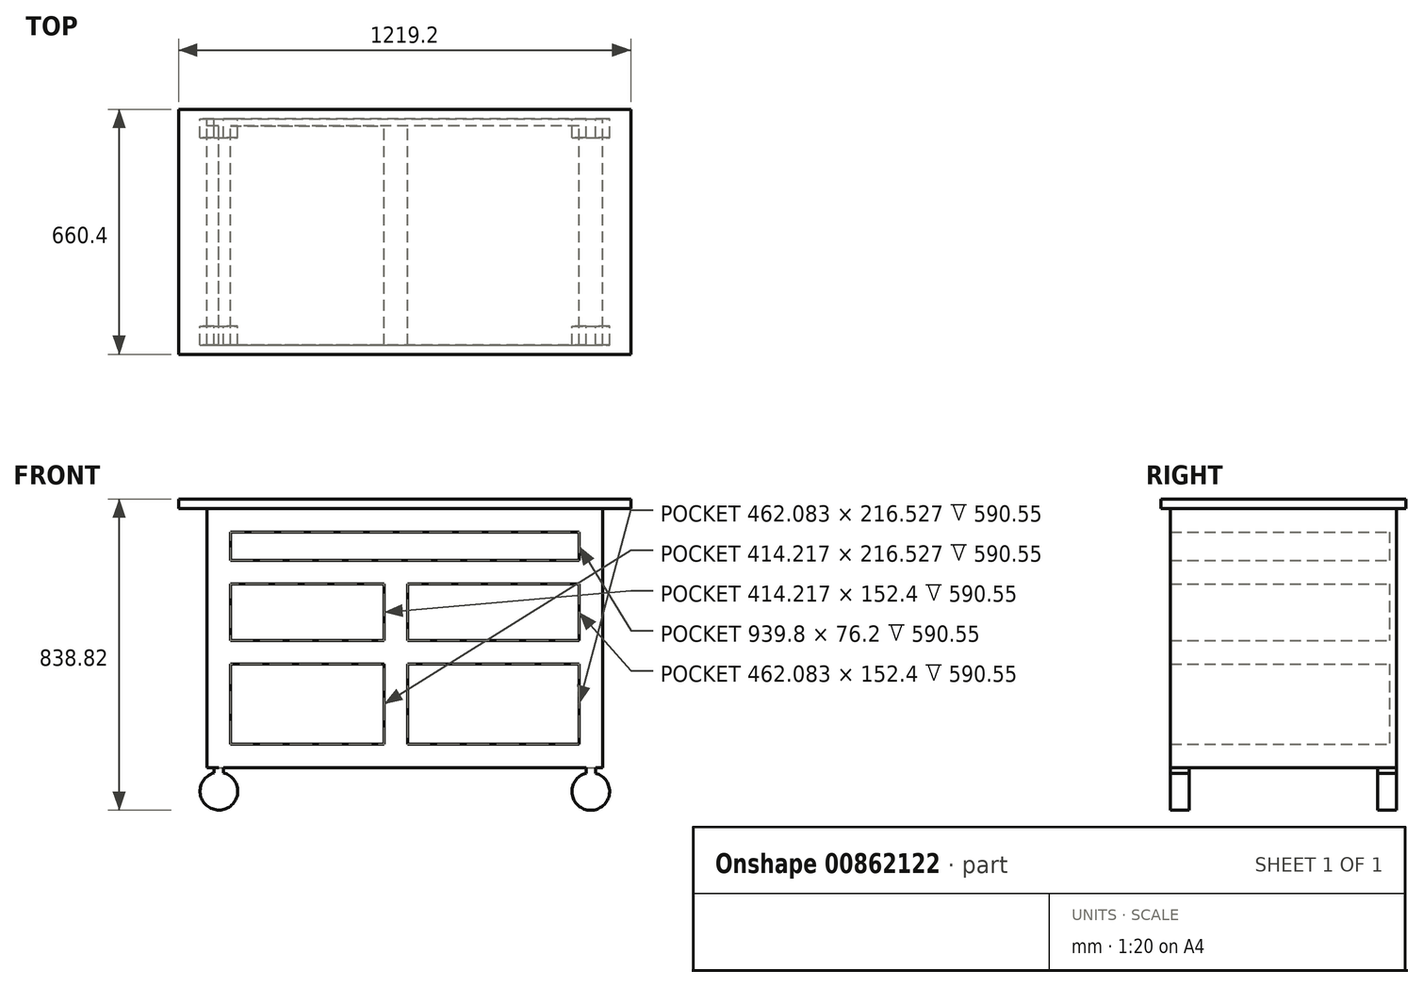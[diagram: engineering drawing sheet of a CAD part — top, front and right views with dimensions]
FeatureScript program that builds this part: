
annotation { "Feature Type Name" : "Feature", "Feature Type Description" : "" }
export const myFeature = defineFeature(function(context is Context, id is Id, definition is map)
    precondition{}
    {
        {
            var Q0;
            Q0=qCreatedBy(makeId("Front.planeOp"),FACE);
            var sketch = newSketch(context, id + "F0", { "sketchPlane" : qUnion([Q0])});
            skLineSegment(sketch, "E0.bottom", {"start": v(533.4, -317.81) * mm, "end": v(-533.4, -317.81) * mm});
            skLineSegment(sketch, "E0.top", {"start": v(533.4, 317.81) * mm, "end": v(-533.4, 317.81) * mm});
            skLineSegment(sketch, "E0.left", {"start": v(533.4, -317.81) * mm, "end": v(533.4, 317.81) * mm});
            skLineSegment(sketch, "E0.right", {"start": v(-533.4, -317.81) * mm, "end": v(-533.4, 317.81) * mm});
            skPoint(sketch, "E0.middle", {"position": v(0, 0) * mm});
            skLineSegment(sketch, "E1.top", {"start": v(469.9, 317.81) * mm, "end": v(-469.9, 317.81) * mm});
            skLineSegment(sketch, "E1.left", {"start": v(469.9, -317.81) * mm, "end": v(469.9, 317.81) * mm});
            skLineSegment(sketch, "E1.right", {"start": v(-469.9, -317.81) * mm, "end": v(-469.9, 317.81) * mm});
            skLineSegment(sketch, "E2.bottom", {"start": v(-533.4, 317.81) * mm, "end": v(533.4, 317.81) * mm});
            skLineSegment(sketch, "E2.top", {"start": v(-533.4, 381.31) * mm, "end": v(533.4, 381.31) * mm});
            skLineSegment(sketch, "E2.left", {"start": v(-533.4, 317.81) * mm, "end": v(-533.4, 381.31) * mm});
            skLineSegment(sketch, "E2.right", {"start": v(533.4, 317.81) * mm, "end": v(533.4, 381.31) * mm});
            skCircle(sketch, "E3", {"center": v(-500.76, -380.69) * mm, "radius": 50.8 * mm});
            skCircle(sketch, "E4", {"center": v(501.65, -381.31) * mm, "radius": 50.8 * mm});
            skLineSegment(sketch, "E5.top", {"start": v(-469.9, -254.31) * mm, "end": v(469.9, -254.31) * mm});
            skLineSegment(sketch, "E5.left", {"start": v(-469.9, -317.81) * mm, "end": v(-469.9, -254.31) * mm});
            skLineSegment(sketch, "E5.right", {"start": v(469.9, -273.37) * mm, "end": v(469.9, -254.31) * mm});
            skLineSegment(sketch, "E6.bottom", {"start": v(-469.9, 241.61) * mm, "end": v(469.9, 241.61) * mm});
            skLineSegment(sketch, "E6.top", {"start": v(-469.9, 178.11) * mm, "end": v(469.9, 178.11) * mm});
            skLineSegment(sketch, "E6.left", {"start": v(-469.9, 241.61) * mm, "end": v(-469.9, 178.11) * mm});
            skLineSegment(sketch, "E6.right", {"start": v(469.9, 241.61) * mm, "end": v(469.9, 178.11) * mm});
            skLineSegment(sketch, "E7.bottom", {"start": v(469.9, 25.71) * mm, "end": v(-469.9, 25.71) * mm});
            skLineSegment(sketch, "E7.top", {"start": v(469.9, -37.79) * mm, "end": v(-469.9, -37.79) * mm});
            skLineSegment(sketch, "E7.left", {"start": v(469.9, 25.71) * mm, "end": v(469.9, -37.79) * mm});
            skLineSegment(sketch, "E7.right", {"start": v(-469.9, 25.71) * mm, "end": v(-469.9, -37.79) * mm});
            skLineSegment(sketch, "E8.bottom", {"start": v(-55.68, 178.11) * mm, "end": v(7.82, 178.11) * mm});
            skLineSegment(sketch, "E8.top", {"start": v(-55.68, -254.31) * mm, "end": v(7.82, -254.31) * mm});
            skLineSegment(sketch, "E8.left", {"start": v(-55.68, 178.11) * mm, "end": v(-55.68, -254.31) * mm});
            skLineSegment(sketch, "E8.right", {"start": v(7.82, 178.11) * mm, "end": v(7.82, -254.31) * mm});
            skLineSegment(sketch, "E9", {"start": v(-501.66, -317.2) * mm, "end": v(-500.76, -380.69) * mm});
            skLineSegment(sketch, "E10", {"start": v(501.65, -317.81) * mm, "end": v(501.65, -381.31) * mm});
            skLineSegment(sketch, "E11", {"start": v(-533.4, -317.81) * mm, "end": v(-501.66, -317.2) * mm});
            skLineSegment(sketch, "E12", {"start": v(533.4, -317.81) * mm, "end": v(501.65, -317.81) * mm});
            skLineSegment(sketch, "E13.bottom", {"start": v(-488.96, -342.6) * mm, "end": v(-514.36, -342.6) * mm});
            skLineSegment(sketch, "E13.top", {"start": v(-488.96, -291.8) * mm, "end": v(-514.36, -291.8) * mm});
            skLineSegment(sketch, "E13.left", {"start": v(-488.96, -342.6) * mm, "end": v(-488.96, -291.8) * mm});
            skLineSegment(sketch, "E13.right", {"start": v(-514.36, -342.6) * mm, "end": v(-514.36, -291.8) * mm});
            skPoint(sketch, "E13.middle", {"position": v(-501.66, -317.2) * mm});
            skLineSegment(sketch, "E14.bottom", {"start": v(514.35, -343.21) * mm, "end": v(488.95, -343.21) * mm});
            skLineSegment(sketch, "E14.top", {"start": v(514.35, -292.41) * mm, "end": v(488.95, -292.41) * mm});
            skLineSegment(sketch, "E14.left", {"start": v(514.35, -343.21) * mm, "end": v(514.35, -292.41) * mm});
            skLineSegment(sketch, "E14.right", {"start": v(488.95, -343.21) * mm, "end": v(488.95, -292.41) * mm});
            skPoint(sketch, "E14.middle", {"position": v(501.65, -317.81) * mm});
            skSolve(sketch);
        }
        {
            var Q0;
            {var subQ1=sQuery(id+"F0.wireOp",EDGE,"E0.right");Q0=makeQuery(id+"F0.imprint","IMPRINT",FACE,{"disambiguationData":[TD([[makeQuery(id+"F0.imprint","IMPRINT",EDGE,{"derivedFrom":subQ1}),-1.0]])]});}
            var Q1;
            Q1=makeQuery(id+"F0.imprint","IMPRINT",FACE,{"disambiguationData":[TD([[makeQuery(id+"F0.imprint","IMPRINT",EDGE,{"derivedFrom":sQuery(id+"F0.wireOp",EDGE,"E2.top")}),-1.0]])]});
            var Q2;
            {var subQ4=sQuery(id+"F0.wireOp",EDGE,"E6.bottom");Q2=makeQuery(id+"F0.imprint","IMPRINT",FACE,{"disambiguationData":[TD([[makeQuery(id+"F0.imprint","IMPRINT",EDGE,{"derivedFrom":subQ4}),-1.0]])]});}
            var Q3;
            {var subQ0=sQuery(id+"F0.wireOp",EDGE,"E7.top");var subQ1=sQuery(id+"F0.wireOp",EDGE,"E1.right");var subQ2=makeQuery(id+"F0.imprint","INTERSECT",VERTEX,{"derivedFrom":[subQ1,subQ0]});Q3=makeQuery(id+"F0.imprint","IMPRINT",FACE,{"disambiguationData":[TD([[makeQuery(id+"F0.imprint","IMPRINT",EDGE,{"disambiguationData":[TD([[subQ2,-1.0]])],"derivedFrom":subQ1}),-1.0]])]});}
            var Q4;
            {var subQ5=sQuery(id+"F0.wireOp",EDGE,"E1.left");var subQ7=makeQuery(id+"F0.imprint","IMPRINT",VERTEX,{"derivedFrom":subQ5});Q4=makeQuery(id+"F0.imprint","IMPRINT",FACE,{"disambiguationData":[TD([[makeQuery(id+"F0.imprint","IMPRINT",EDGE,{"disambiguationData":[TD([[subQ7,1.0]])],"derivedFrom":subQ5}),1.0]])]});}
            var Q5;
            {var subQ0=sQuery(id+"F0.wireOp",EDGE,"E8.right");var subQ1=sQuery(id+"F0.wireOp",EDGE,"E5.top");var subQ2=makeQuery(id+"F0.imprint","INTERSECT",VERTEX,{"derivedFrom":[subQ1,subQ0]});Q5=makeQuery(id+"F0.imprint","IMPRINT",FACE,{"disambiguationData":[TD([[makeQuery(id+"F0.imprint","IMPRINT",EDGE,{"disambiguationData":[TD([[subQ2,1.0]])],"derivedFrom":subQ1}),1.0]])]});}
            var Q6;
            {var subQ0=sQuery(id+"F0.wireOp",EDGE,"E8.left");var subQ1=sQuery(id+"F0.wireOp",EDGE,"E7.bottom");var subQ2=makeQuery(id+"F0.imprint","INTERSECT",VERTEX,{"derivedFrom":[subQ1,subQ0]});Q6=makeQuery(id+"F0.imprint","IMPRINT",FACE,{"disambiguationData":[TD([[makeQuery(id+"F0.imprint","IMPRINT",EDGE,{"disambiguationData":[TD([[subQ2,1.0]])],"derivedFrom":subQ1}),1.0]])]});}
            var Q7;
            {var subQ0=sQuery(id+"F0.wireOp",EDGE,"E8.right");var subQ1=sQuery(id+"F0.wireOp",EDGE,"E6.top");var subQ2=makeQuery(id+"F0.imprint","INTERSECT",VERTEX,{"derivedFrom":[subQ1,subQ0]});Q7=makeQuery(id+"F0.imprint","IMPRINT",FACE,{"disambiguationData":[TD([[makeQuery(id+"F0.imprint","IMPRINT",EDGE,{"disambiguationData":[TD([[subQ2,1.0]])],"derivedFrom":subQ1}),-1.0]])]});}
            var Q8;
            {var subQ0=sQuery(id+"F0.wireOp",EDGE,"E7.bottom");var subQ1=sQuery(id+"F0.wireOp",EDGE,"E1.left");var subQ2=makeQuery(id+"F0.imprint","INTERSECT",VERTEX,{"derivedFrom":[subQ1,subQ0]});Q8=makeQuery(id+"F0.imprint","IMPRINT",FACE,{"disambiguationData":[TD([[makeQuery(id+"F0.imprint","IMPRINT",EDGE,{"disambiguationData":[TD([[subQ2,1.0]])],"derivedFrom":subQ1}),1.0]])]});}
            var Q9;
            {var subQ12=sQuery(id+"F0.wireOp",EDGE,"E0.left");Q9=makeQuery(id+"F0.imprint","IMPRINT",FACE,{"disambiguationData":[TD([[makeQuery(id+"F0.imprint","IMPRINT",EDGE,{"derivedFrom":subQ12}),1.0]])]});}
            var Q10;
            {var subQ1=sQuery(id+"F0.wireOp",EDGE,"E14.top");Q10=makeQuery(id+"F0.imprint","IMPRINT",FACE,{"disambiguationData":[TD([[makeQuery(id+"F0.imprint","IMPRINT",EDGE,{"derivedFrom":subQ1}),1.0]])]});}
            var Q11;
            {var subQ0=sQuery(id+"F0.wireOp",EDGE,"E13.top");Q11=makeQuery(id+"F0.imprint","IMPRINT",FACE,{"disambiguationData":[TD([[makeQuery(id+"F0.imprint","IMPRINT",EDGE,{"derivedFrom":subQ0}),1.0]])]});}
            extrude(context, id + "F1", {"entities" : qUnion([Q0, Q1, Q2, Q3, Q4, Q5, Q6, Q7, Q8, Q9, Q10, Q11]), "depth" : 609.6 * mm, "offsetDistance" : 25.4 * mm});
        }
        {
            var Q0;
            {var subQ2=sQuery(id+"F0.wireOp",EDGE,"E13.left");var subQ4=sQuery(id+"F0.wireOp",EDGE,"E3");var subQ5=makeQuery(id+"F0.imprint","INTERSECT",VERTEX,{"derivedFrom":[subQ4,subQ2]});Q0=makeQuery(id+"F0.imprint","IMPRINT",FACE,{"disambiguationData":[TD([[makeQuery(id+"F0.imprint","IMPRINT",EDGE,{"disambiguationData":[TD([[subQ5,1.0]])],"derivedFrom":subQ4}),1.0]])]});}
            var Q1;
            {var subQ0=sQuery(id+"F0.wireOp",EDGE,"E13.right");var subQ1=sQuery(id+"F0.wireOp",EDGE,"E3");var subQ2=makeQuery(id+"F0.imprint","INTERSECT",VERTEX,{"derivedFrom":[subQ1,subQ0]});Q1=makeQuery(id+"F0.imprint","IMPRINT",FACE,{"disambiguationData":[TD([[makeQuery(id+"F0.imprint","IMPRINT",EDGE,{"disambiguationData":[TD([[subQ2,1.0]])],"derivedFrom":subQ1}),1.0]])]});}
            var Q2;
            {var subQ0=sQuery(id+"F0.wireOp",EDGE,"E9");var subQ1=sQuery(id+"F0.wireOp",EDGE,"E0.bottom");var subQ2=makeQuery(id+"F0.imprint","INTERSECT",VERTEX,{"derivedFrom":[subQ1,subQ0]});Q2=makeQuery(id+"F0.imprint","IMPRINT",FACE,{"disambiguationData":[TD([[makeQuery(id+"F0.imprint","IMPRINT",EDGE,{"disambiguationData":[TD([[subQ2,-1.0]])],"derivedFrom":subQ1}),1.0]])]});}
            var Q3;
            {var subQ0=sQuery(id+"F0.wireOp",EDGE,"E9");var subQ1=sQuery(id+"F0.wireOp",EDGE,"E0.bottom");var subQ2=makeQuery(id+"F0.imprint","INTERSECT",VERTEX,{"derivedFrom":[subQ1,subQ0]});Q3=makeQuery(id+"F0.imprint","IMPRINT",FACE,{"disambiguationData":[TD([[makeQuery(id+"F0.imprint","IMPRINT",EDGE,{"disambiguationData":[TD([[subQ2,1.0]])],"derivedFrom":subQ1}),1.0]])]});}
            var Q4;
            {var subQ0=sQuery(id+"F0.wireOp",EDGE,"E13.left");var subQ1=sQuery(id+"F0.wireOp",EDGE,"E3");var subQ2=makeQuery(id+"F0.imprint","INTERSECT",VERTEX,{"derivedFrom":[subQ1,subQ0]});Q4=makeQuery(id+"F0.imprint","IMPRINT",FACE,{"disambiguationData":[TD([[makeQuery(id+"F0.imprint","IMPRINT",EDGE,{"disambiguationData":[TD([[subQ2,-1.0]])],"derivedFrom":subQ1}),1.0]])]});}
            var Q5;
            {var subQ2=sQuery(id+"F0.wireOp",EDGE,"E14.left");var subQ4=sQuery(id+"F0.wireOp",EDGE,"E4");var subQ5=makeQuery(id+"F0.imprint","INTERSECT",VERTEX,{"derivedFrom":[subQ4,subQ2]});Q5=makeQuery(id+"F0.imprint","IMPRINT",FACE,{"disambiguationData":[TD([[makeQuery(id+"F0.imprint","IMPRINT",EDGE,{"disambiguationData":[TD([[subQ5,1.0]])],"derivedFrom":subQ4}),1.0]])]});}
            var Q6;
            {var subQ0=sQuery(id+"F0.wireOp",EDGE,"E14.left");var subQ1=sQuery(id+"F0.wireOp",EDGE,"E4");var subQ2=makeQuery(id+"F0.imprint","INTERSECT",VERTEX,{"derivedFrom":[subQ1,subQ0]});Q6=makeQuery(id+"F0.imprint","IMPRINT",FACE,{"disambiguationData":[TD([[makeQuery(id+"F0.imprint","IMPRINT",EDGE,{"disambiguationData":[TD([[subQ2,-1.0]])],"derivedFrom":subQ1}),1.0]])]});}
            var Q7;
            {var subQ0=sQuery(id+"F0.wireOp",EDGE,"E14.right");var subQ1=sQuery(id+"F0.wireOp",EDGE,"E0.bottom");var subQ2=makeQuery(id+"F0.imprint","INTERSECT",VERTEX,{"derivedFrom":[subQ1,subQ0]});Q7=makeQuery(id+"F0.imprint","IMPRINT",FACE,{"disambiguationData":[TD([[makeQuery(id+"F0.imprint","IMPRINT",EDGE,{"disambiguationData":[TD([[subQ2,1.0]])],"derivedFrom":subQ1}),1.0]])]});}
            var Q8;
            {var subQ0=sQuery(id+"F0.wireOp",EDGE,"E14.left");var subQ1=sQuery(id+"F0.wireOp",EDGE,"E0.bottom");var subQ2=makeQuery(id+"F0.imprint","INTERSECT",VERTEX,{"derivedFrom":[subQ1,subQ0]});Q8=makeQuery(id+"F0.imprint","IMPRINT",FACE,{"disambiguationData":[TD([[makeQuery(id+"F0.imprint","IMPRINT",EDGE,{"disambiguationData":[TD([[subQ2,-1.0]])],"derivedFrom":subQ1}),1.0]])]});}
            var Q9;
            {var subQ0=sQuery(id+"F0.wireOp",EDGE,"E14.right");var subQ1=sQuery(id+"F0.wireOp",EDGE,"E4");var subQ2=makeQuery(id+"F0.imprint","INTERSECT",VERTEX,{"derivedFrom":[subQ1,subQ0]});Q9=makeQuery(id+"F0.imprint","IMPRINT",FACE,{"disambiguationData":[TD([[makeQuery(id+"F0.imprint","IMPRINT",EDGE,{"disambiguationData":[TD([[subQ2,1.0]])],"derivedFrom":subQ1}),1.0]])]});}
            extrude(context, id + "F2", {"entities" : qUnion([Q0, Q1, Q2, Q3, Q4, Q5, Q6, Q7, Q8, Q9]), "operationType" : NewBodyOperationType.ADD, "depth" : 609.6 * mm, "offsetDistance" : 25.4 * mm});
        }
        {
            var Q0;
            Q0=makeQuery(id+"F1.opExtrude","SWEPT_FACE",FACE,{"disambiguationData":[OSD([sQuery(id+"F0.wireOp",EDGE,"E0.left"),sQuery(id+"F0.wireOp",EDGE,"E2.right")])]});
            cPlane(context, id + "F3", {"entities" : qUnion([Q0]), "cplaneType" : CPlaneType.OFFSET, "offset" : 127 * mm, "width" : 152.4 * mm, "height" : 152.4 * mm});
        }
        {
            var Q0;
            Q0=qCreatedBy(id+"F3.planeOp",FACE);
            var sketch = newSketch(context, id + "F4", { "sketchPlane" : qUnion([Q0])});
            skLineSegment(sketch, "E15.bottom", {"start": v(-609.6, -317.81) * mm, "end": v(-558.8, -317.81) * mm});
            skLineSegment(sketch, "E15.top", {"start": v(-609.6, -353.91) * mm, "end": v(-558.8, -353.91) * mm});
            skLineSegment(sketch, "E15.left", {"start": v(-609.6, -317.81) * mm, "end": v(-609.6, -353.91) * mm});
            skLineSegment(sketch, "E15.right", {"start": v(-558.8, -317.81) * mm, "end": v(-558.8, -353.91) * mm});
            skLineSegment(sketch, "E16.bottom", {"start": v(0, -317.81) * mm, "end": v(-50.8, -317.81) * mm});
            skLineSegment(sketch, "E16.top", {"start": v(0, -353.91) * mm, "end": v(-50.8, -353.91) * mm});
            skLineSegment(sketch, "E16.left", {"start": v(0, -317.81) * mm, "end": v(0, -353.91) * mm});
            skLineSegment(sketch, "E16.right", {"start": v(-50.8, -317.81) * mm, "end": v(-50.8, -353.91) * mm});
            skLineSegment(sketch, "E17.bottom", {"start": v(-50.8, -317.81) * mm, "end": v(-558.8, -317.81) * mm});
            skLineSegment(sketch, "E17.top", {"start": v(-50.8, -456.82) * mm, "end": v(-558.8, -456.82) * mm});
            skLineSegment(sketch, "E17.left", {"start": v(-50.8, -317.81) * mm, "end": v(-50.8, -456.82) * mm});
            skLineSegment(sketch, "E17.right", {"start": v(-558.8, -317.81) * mm, "end": v(-558.8, -456.82) * mm});
            skSolve(sketch);
        }
        {
            var Q0;
            Q0=makeQuery(id+"F4.imprint","IMPRINT",FACE,{"disambiguationData":[TD([[makeQuery(id+"F4.imprint","IMPRINT",EDGE,{"derivedFrom":sQuery(id+"F4.wireOp",EDGE,"E15.right")}),1.0]])]});
            extrude(context, id + "F5", {"entities" : qUnion([Q0]), "operationType" : NewBodyOperationType.REMOVE, "oppositeDirection" : true, "depth" : 1242.06 * mm, "offsetDistance" : 25.4 * mm});
        }
        {
            var Q0;
            Q0=makeQuery(id+"F1.opExtrude","SWEPT_FACE",FACE,{"disambiguationData":[OSD([sQuery(id+"F0.wireOp",EDGE,"E0.right"),sQuery(id+"F0.wireOp",EDGE,"E2.left")])]});
            var sketch = newSketch(context, id + "F6", { "sketchPlane" : qUnion([Q0])});
            skLineSegment(sketch, "E18.bottom", {"start": v(0, 381.31) * mm, "end": v(19.05, 381.31) * mm});
            skLineSegment(sketch, "E18.top", {"start": v(0, -317.81) * mm, "end": v(19.05, -317.81) * mm});
            skLineSegment(sketch, "E18.left", {"start": v(0, 381.31) * mm, "end": v(0, -317.81) * mm});
            skLineSegment(sketch, "E18.right", {"start": v(19.05, 381.31) * mm, "end": v(19.05, -317.81) * mm});
            skSolve(sketch);
        }
        {
            var Q0;
            Q0=makeQuery(id+"F6.imprint","IMPRINT",FACE,{"disambiguationData":[TD([[makeQuery(id+"F6.imprint","IMPRINT",EDGE,{"derivedFrom":sQuery(id+"F6.wireOp",EDGE,"E18.bottom")}),1.0]])]});
            extrude(context, id + "F7", {"entities" : qUnion([Q0]), "operationType" : NewBodyOperationType.ADD, "oppositeDirection" : true, "depth" : 1066.8 * mm, "offsetDistance" : 25.4 * mm});
        }
        {
            var Q0;
            Q0=makeQuery(id+"F1.opExtrude","SWEPT_FACE",FACE,{"disambiguationData":[OSD([sQuery(id+"F0.wireOp",EDGE,"E2.top")])]});
            var sketch = newSketch(context, id + "F8", { "sketchPlane" : qUnion([Q0])});
            skLineSegment(sketch, "E19.bottom", {"start": v(-609.6, -635) * mm, "end": v(609.6, -635) * mm});
            skLineSegment(sketch, "E19.top", {"start": v(-609.6, 25.4) * mm, "end": v(609.6, 25.4) * mm});
            skLineSegment(sketch, "E19.left", {"start": v(-609.6, -635) * mm, "end": v(-609.6, 25.4) * mm});
            skLineSegment(sketch, "E19.right", {"start": v(609.6, -635) * mm, "end": v(609.6, 25.4) * mm});
            skPoint(sketch, "E19.middle", {"position": v(0, -304.8) * mm});
            skPoint(sketch, "E19.middle.positionSnap0", {"position": v(-533.4, -304.8) * mm});
            skPoint(sketch, "E19.centerSnap0", {"position": v(-533.4, -304.8) * mm});
            skSolve(sketch);
        }
        {
            var Q0;
            Q0=makeQuery(id+"F8.imprint","IMPRINT",FACE,{"disambiguationData":[TD([[makeQuery(id+"F8.imprint","IMPRINT",EDGE,{"derivedFrom":sQuery(id+"F8.wireOp",EDGE,"E19.bottom")}),1.0]])]});
            var Q1;
            {var subQ0=sQuery(id+"F0.wireOp",EDGE,"E2.top");Q1=makeQuery(id+"F8.imprint","IMPRINT",FACE,{"disambiguationData":[TD([[makeQuery(id+"F8.imprint","IMPRINT",EDGE,{"derivedFrom":makeQuery(id+"F1.opExtrude","CAP_EDGE",EDGE,{"disambiguationData":[OSD([subQ0])],"isStart":true})}),-1.0]])]});}
            extrude(context, id + "F9", {"entities" : qUnion([Q0, Q1]), "depth" : 25.4 * mm, "offsetDistance" : 25.4 * mm});
        }
    });
